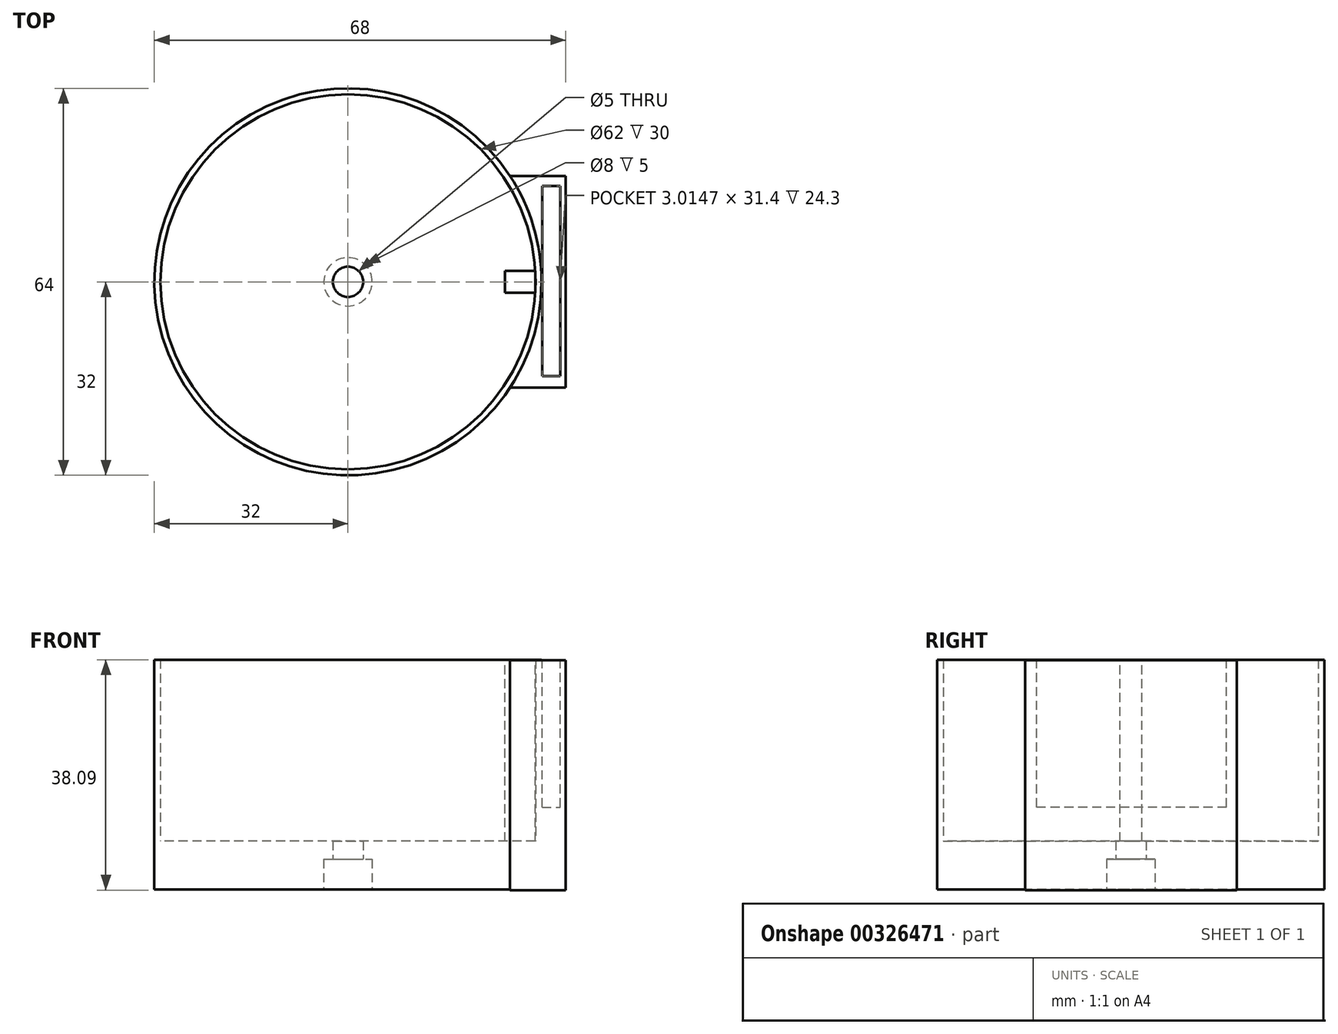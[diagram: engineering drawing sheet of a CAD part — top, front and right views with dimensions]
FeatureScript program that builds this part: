
annotation { "Feature Type Name" : "Feature", "Feature Type Description" : "" }
export const myFeature = defineFeature(function(context is Context, id is Id, definition is map)
    precondition{}
    {
        {
            var Q0;
            Q0=qCreatedBy(makeId("Top.planeOp"),FACE);
            var sketch = newSketch(context, id + "F0", { "sketchPlane" : qUnion([Q0])});
            skCircle(sketch, "E0", {"center": v(0, 0) * mm, "radius": 31 * mm});
            skCircle(sketch, "E1", {"center": v(0, 0) * mm, "radius": 32 * mm});
            skSolve(sketch);
        }
        {
            var Q0;
            Q0 = qSketchRegion(id + "F0", true);
            extrude(context, id + "F1", {"entities" : qUnion([Q0]), "depth" : 30 * mm});
        }
        {
            var Q0;
            Q0=qCreatedBy(makeId("Right.planeOp"),FACE);
            cPlane(context, id + "F2", {"entities" : qUnion([Q0]), "cplaneType" : CPlaneType.OFFSET, "offset" : 32 * mm, "width" : 150 * mm, "height" : 150 * mm});
        }
        {
            var Q0;
            Q0=qCreatedBy(id+"F2.planeOp",FACE);
            var sketch = newSketch(context, id + "F3", { "sketchPlane" : qUnion([Q0])});
            skLineSegment(sketch, "E2.bottom", {"start": v(-17.5, 29.9) * mm, "end": v(17.5, 29.9) * mm});
            skLineSegment(sketch, "E2.top", {"start": v(-17.5, -0.1) * mm, "end": v(17.5, -0.1) * mm});
            skLineSegment(sketch, "E2.left", {"start": v(-17.5, 29.9) * mm, "end": v(-17.5, -0.1) * mm});
            skLineSegment(sketch, "E2.right", {"start": v(17.5, 29.9) * mm, "end": v(17.5, -0.1) * mm});
            skPoint(sketch, "E2.middle", {"position": v(0, 14.9) * mm});
            skSolve(sketch);
        }
        {
            var Q0;
            Q0 = qSketchRegion(id + "F3", true);
            extrude(context, id + "F4", {"entities" : qUnion([Q0]), "depth" : 4 * mm});
        }
        {
            var Q0;
            Q0=makeQuery(id+"F4.opExtrude","CAP_FACE",FACE,{"disambiguationData":[OSD([sQuery(id+"F3.wireOp",EDGE,"E2.bottom"),sQuery(id+"F3.wireOp",EDGE,"E2.top"),sQuery(id+"F3.wireOp",EDGE,"E2.left"),sQuery(id+"F3.wireOp",EDGE,"E2.right")])],"isStart":true});
            extrude(context, id + "F5", {"entities" : qUnion([Q0]), "operationType" : NewBodyOperationType.ADD, "depth" : 5.5 * mm});
        }
        {
            var Q0;
            Q0=makeQuery(id+"F1.opExtrude","CAP_FACE",FACE,{"disambiguationData":[OSD([sQuery(id+"F0.wireOp",EDGE,"E0"),sQuery(id+"F0.wireOp",EDGE,"E1")])],"isStart":false});
            var sketch = newSketch(context, id + "F6", { "sketchPlane" : qUnion([Q0])});
            skCircle(sketch, "E3", {"center": v(0, 0) * mm, "radius": 31 * mm});
            skSolve(sketch);
        }
        {
            var Q0;
            Q0=makeQuery(id+"F6.imprint","IMPRINT",FACE,{"disambiguationData":[TD([[makeQuery(id+"F6.imprint","IMPRINT",EDGE,{"derivedFrom":sQuery(id+"F6.wireOp",EDGE,"E3")}),1.0]])]});
            extrude(context, id + "F7", {"entities" : qUnion([Q0]), "operationType" : NewBodyOperationType.REMOVE, "oppositeDirection" : true, "depth" : 40 * mm});
        }
        {
            var Q0;
            Q0=qCreatedBy(makeId("Top.planeOp"),FACE);
            var sketch = newSketch(context, id + "F8", { "sketchPlane" : qUnion([Q0])});
            skCircle(sketch, "E4", {"center": v(0, 0) * mm, "radius": 32 * mm});
            skSolve(sketch);
        }
        {
            var Q0;
            Q0 = qSketchRegion(id + "F8", true);
            extrude(context, id + "F9", {"entities" : qUnion([Q0]), "operationType" : NewBodyOperationType.ADD, "oppositeDirection" : true, "depth" : 3 * mm});
        }
        {
            var Q0;
            Q0=makeQuery(id+"F9.opExtrude","CAP_FACE",FACE,{"disambiguationData":[OSD([sQuery(id+"F8.wireOp",EDGE,"E4")])],"isStart":false});
            var sketch = newSketch(context, id + "F10", { "sketchPlane" : qUnion([Q0])});
            skCircle(sketch, "E5", {"center": v(0, 0) * mm, "radius": 2.5 * mm});
            skSolve(sketch);
        }
        {
            var Q0;
            Q0=makeQuery(id+"F10.imprint","IMPRINT",FACE,{"disambiguationData":[TD([[makeQuery(id+"F10.imprint","IMPRINT",EDGE,{"derivedFrom":sQuery(id+"F10.wireOp",EDGE,"E5")}),1.0]])]});
            extrude(context, id + "F11", {"entities" : qUnion([Q0]), "operationType" : NewBodyOperationType.REMOVE, "oppositeDirection" : true, "depth" : 25 * mm});
        }
        {
            var Q0;
            Q0=makeQuery(id+"F9.opExtrude","CAP_FACE",FACE,{"disambiguationData":[OSD([sQuery(id+"F8.wireOp",EDGE,"E4")])],"isStart":false});
            extrude(context, id + "F12", {"entities" : qUnion([Q0]), "operationType" : NewBodyOperationType.ADD, "depth" : 5 * mm});
        }
        {
            var Q0;
            Q0=makeQuery(id+"F12.opExtrude","CAP_FACE",FACE,{"disambiguationData":[OSD([sQuery(id+"F8.wireOp",EDGE,"E4")])],"isStart":false});
            var sketch = newSketch(context, id + "F13", { "sketchPlane" : qUnion([Q0])});
            skCircle(sketch, "E6", {"center": v(0, 0) * mm, "radius": 4 * mm});
            skSolve(sketch);
        }
        {
            var Q0;
            Q0=makeQuery(id+"F13.imprint","IMPRINT",FACE,{"disambiguationData":[TD([[makeQuery(id+"F13.imprint","IMPRINT",EDGE,{"derivedFrom":sQuery(id+"F13.wireOp",EDGE,"E6")}),1.0]])]});
            extrude(context, id + "F14", {"entities" : qUnion([Q0]), "operationType" : NewBodyOperationType.REMOVE, "oppositeDirection" : true, "depth" : 5 * mm});
        }
        {
            var Q0;
            {var subQ0=sQuery(id+"F3.wireOp",EDGE,"E2.top");Q0=makeQuery(id+"F5.boolean.opBoolean","MERGE",FACE,{"derivedFrom":[makeQuery(id+"F4.opExtrude","SWEPT_FACE",FACE,{"disambiguationData":[OSD([subQ0])]}),makeQuery(id+"F5.opExtrude","SWEPT_FACE",FACE,{"disambiguationData":[OSD([subQ0])]})]});}
            extrude(context, id + "F15", {"entities" : qUnion([Q0]), "operationType" : NewBodyOperationType.ADD, "depth" : 8 * mm});
        }
        {
            var Q0;
            Q0=makeQuery(id+"F4.opExtrude","SWEPT_FACE",FACE,{"disambiguationData":[OSD([sQuery(id+"F3.wireOp",EDGE,"E2.bottom")])]});
            var sketch = newSketch(context, id + "F16", { "sketchPlane" : qUnion([Q0])});
            skLineSegment(sketch, "E7.bottom", {"start": v(32.07, 15.81) * mm, "end": v(35.09, 15.81) * mm});
            skLineSegment(sketch, "E7.top", {"start": v(32.07, -15.59) * mm, "end": v(35.09, -15.59) * mm});
            skLineSegment(sketch, "E7.left", {"start": v(32.07, 15.81) * mm, "end": v(32.07, -15.59) * mm});
            skLineSegment(sketch, "E7.right", {"start": v(35.09, 6.7) * mm, "end": v(35.09, -15.59) * mm});
            skLineSegment(sketch, "E8.left", {"start": v(35.09, 13.5) * mm, "end": v(35.09, -14.74) * mm});
            skLineSegment(sketch, "E9", {"start": v(35.09, 15.81) * mm, "end": v(35.09, 13.5) * mm});
            skLineSegment(sketch, "E10.left", {"start": v(35.09, 14.66) * mm, "end": v(35.09, -12.34) * mm});
            skLineSegment(sketch, "E11", {"start": v(37.05, 13.63) * mm, "end": v(37.05, -13.37) * mm});
            skLineSegment(sketch, "E12", {"start": v(37.05, 13.63) * mm, "end": v(35.09, 13.63) * mm});
            skLineSegment(sketch, "E13", {"start": v(37.05, -13.37) * mm, "end": v(35.09, -13.37) * mm});
            skSolve(sketch);
        }
        {
            var Q0;
            Q0=makeQuery(id+"F16.imprint","IMPRINT",FACE,{"disambiguationData":[TD([[makeQuery(id+"F16.imprint","IMPRINT",EDGE,{"derivedFrom":sQuery(id+"F16.wireOp",EDGE,"E7.bottom")}),-1.0]])]});
            var Q1;
            {var subQ1=sQuery(id+"F16.wireOp",EDGE,"E10.left");var subQ5=makeQuery(id+"F16.imprint","IMPRINT",VERTEX,{"derivedFrom":subQ1});Q1=makeQuery(id+"F16.imprint","IMPRINT",FACE,{"disambiguationData":[TD([[makeQuery(id+"F16.imprint","IMPRINT",EDGE,{"disambiguationData":[TD([[subQ5,1.0]])],"derivedFrom":subQ1}),1.0]])]});}
            extrude(context, id + "F17", {"entities" : qUnion([Q0, Q1]), "operationType" : NewBodyOperationType.REMOVE, "oppositeDirection" : true, "depth" : 24.3 * mm});
        }
        {
            var Q0;
            Q0=makeQuery(id+"F1.opExtrude","CAP_FACE",FACE,{"disambiguationData":[OSD([sQuery(id+"F0.wireOp",EDGE,"E0"),sQuery(id+"F0.wireOp",EDGE,"E1")])],"isStart":false});
            var sketch = newSketch(context, id + "F18", { "sketchPlane" : qUnion([Q0])});
            skLineSegment(sketch, "E14.bottom", {"start": v(30.95, 1.8) * mm, "end": v(25.95, 1.8) * mm});
            skLineSegment(sketch, "E14.top", {"start": v(30.95, -1.8) * mm, "end": v(25.95, -1.8) * mm});
            skLineSegment(sketch, "E14.left", {"start": v(30.95, 1.8) * mm, "end": v(30.95, -1.8) * mm});
            skLineSegment(sketch, "E14.right", {"start": v(25.95, 1.8) * mm, "end": v(25.95, -1.8) * mm});
            skPoint(sketch, "E14.middle", {"position": v(28.45, 0) * mm});
            skSolve(sketch);
        }
        {
            var Q0;
            Q0=makeQuery(id+"F18.imprint","IMPRINT",FACE,{"disambiguationData":[TD([[makeQuery(id+"F18.imprint","IMPRINT",EDGE,{"derivedFrom":sQuery(id+"F18.wireOp",EDGE,"E14.bottom")}),1.0]])]});
            extrude(context, id + "F19", {"entities" : qUnion([Q0]), "oppositeDirection" : true, "depth" : 30 * mm});
        }
    });
